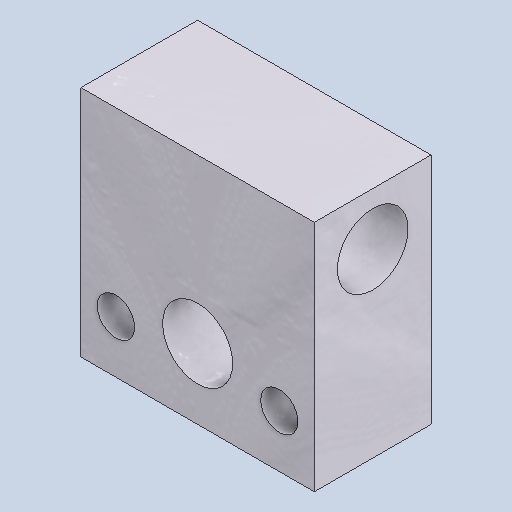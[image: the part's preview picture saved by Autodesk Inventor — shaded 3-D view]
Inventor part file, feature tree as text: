
AUTODESK INVENTOR PART (.ipt)
format: ipt  version: 2022 (Build 260153070, 153G)  size: 204,800 bytes
history: native  units: mm
features: extrude x3, sketch x3
ambient origin geometry x8: Origin, YZ Plane, XZ Plane, XY Plane, X Axis, Y Axis, Z Axis, Center Point
bodies: Solid1 (feature_tree)
feature tree (6):
  extrude  "Extrusion1"  Depth=10.0mm
  sketch  "Sketch2"  dims[d2=10.0mm d3=10.0mm]
  extrude  "Extrusion2"  Depth=10.0mm
  extrude  "Extrusion3"  Depth=10.0mm
  sketch  "Sketch1"  dims[d0=20.0mm d1=10.0mm]
  sketch  "Sketch3"  dims[d4=10.0mm d5=0.0mm d6=6.0mm d7=4.0mm d8=3.2mm d9=7.0mm d10=5.5mm d11=6.05mm d12=5.0mm d13=15.5mm d14=20.0mm d15=0.0mm d16=10.0mm d17=0.0mm]
